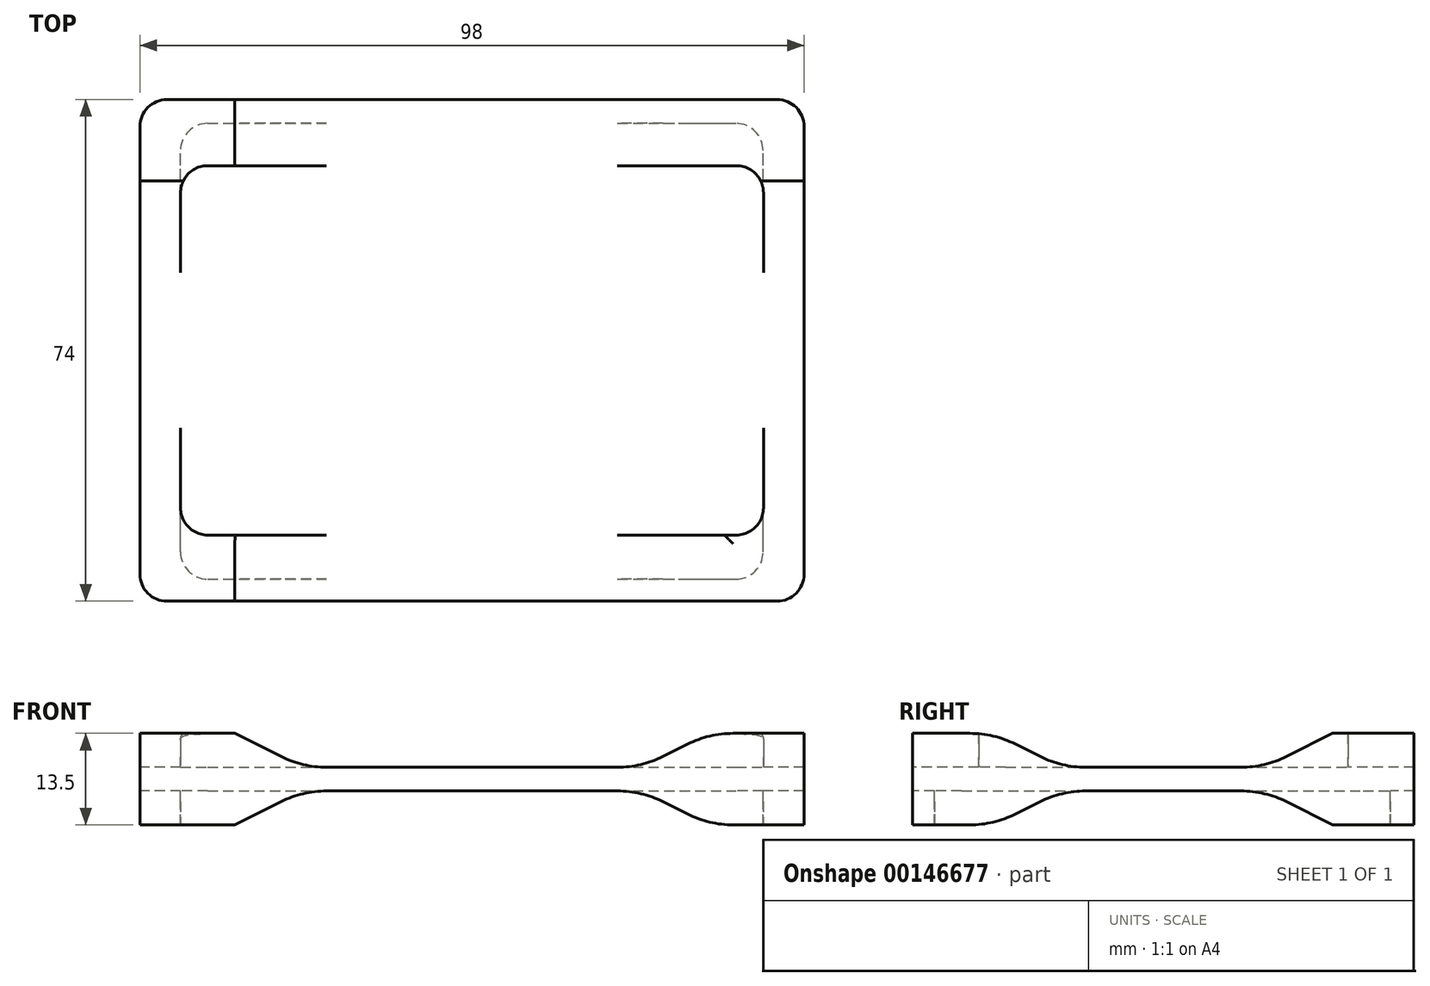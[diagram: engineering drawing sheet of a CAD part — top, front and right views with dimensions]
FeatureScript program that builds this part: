
annotation { "Feature Type Name" : "Feature", "Feature Type Description" : "" }
export const myFeature = defineFeature(function(context is Context, id is Id, definition is map)
    precondition{}
    {
        {
            var Q0;
            Q0=qCreatedBy(makeId("Top.planeOp"),FACE);
            var sketch = newSketch(context, id + "F0", { "sketchPlane" : qUnion([Q0])});
            skLineSegment(sketch, "E0.bottom", {"start": v(4, 0) * mm, "end": v(82, 0) * mm});
            skLineSegment(sketch, "E0.top", {"start": v(4, 54.5) * mm, "end": v(82, 54.5) * mm});
            skLineSegment(sketch, "E0.left", {"start": v(0, 4) * mm, "end": v(0, 50.5) * mm});
            skLineSegment(sketch, "E0.right", {"start": v(86, 4) * mm, "end": v(86, 50.5) * mm});
            skPoint(sketch, "E1.visualSharp", {"position": v(0, 54.5) * mm});
            skArc(sketch, "E1.filletArc", {"start": v(4, 54.5) * mm, "mid": v(1.17, 53.33) * mm, "end": v(0, 50.5) * mm});
            skPoint(sketch, "E2.visualSharp", {"position": v(86, 54.5) * mm});
            skArc(sketch, "E2.filletArc", {"start": v(86, 50.5) * mm, "mid": v(84.83, 53.33) * mm, "end": v(82, 54.5) * mm});
            skPoint(sketch, "E3.visualSharp", {"position": v(86, 0) * mm});
            skArc(sketch, "E3.filletArc", {"start": v(82, 0) * mm, "mid": v(84.83, 1.17) * mm, "end": v(86, 4) * mm});
            skPoint(sketch, "E4.visualSharp", {"position": v(0, 0) * mm});
            skArc(sketch, "E4.filletArc", {"start": v(0, 4) * mm, "mid": v(1.17, 1.17) * mm, "end": v(4, 0) * mm});
            skSolve(sketch);
        }
        {
            var Q0;
            Q0=qCreatedBy(makeId("Top.planeOp"),FACE);
            var sketch = newSketch(context, id + "F1", { "sketchPlane" : qUnion([Q0])});
            skLineSegment(sketch, "E5", {"start": v(0, 0) * mm, "end": v(0, -9.75) * mm, "construction": true});
            skLineSegment(sketch, "E6", {"start": v(0, -9.75) * mm, "end": v(-6, -9.75) * mm, "construction": true});
            skLineSegment(sketch, "E7.bottom", {"start": v(-2, -9.75) * mm, "end": v(88, -9.75) * mm});
            skLineSegment(sketch, "E7.top", {"start": v(-2, 64.25) * mm, "end": v(88, 64.25) * mm});
            skLineSegment(sketch, "E7.left", {"start": v(-6, -5.75) * mm, "end": v(-6, 60.25) * mm});
            skLineSegment(sketch, "E7.right", {"start": v(92, -5.75) * mm, "end": v(92, 60.25) * mm});
            skPoint(sketch, "E8.0", {"position": v(86, 54.5) * mm});
            skLineSegment(sketch, "E9", {"start": v(86, 54.5) * mm, "end": v(86, 64.25) * mm, "construction": true});
            skLineSegment(sketch, "E10", {"start": v(86, 64.25) * mm, "end": v(92, 64.25) * mm, "construction": true});
            skPoint(sketch, "E11.visualSharp", {"position": v(-6, 64.25) * mm});
            skArc(sketch, "E11.filletArc", {"start": v(-2, 64.25) * mm, "mid": v(-4.83, 63.08) * mm, "end": v(-6, 60.25) * mm});
            skPoint(sketch, "E12.visualSharp", {"position": v(92, 64.25) * mm});
            skArc(sketch, "E12.filletArc", {"start": v(92, 60.25) * mm, "mid": v(90.83, 63.08) * mm, "end": v(88, 64.25) * mm});
            skPoint(sketch, "E13.visualSharp", {"position": v(92, -9.75) * mm});
            skArc(sketch, "E13.filletArc", {"start": v(88, -9.75) * mm, "mid": v(90.83, -8.58) * mm, "end": v(92, -5.75) * mm});
            skPoint(sketch, "E14.visualSharp", {"position": v(-6, -9.75) * mm});
            skArc(sketch, "E14.filletArc", {"start": v(-6, -5.75) * mm, "mid": v(-4.83, -8.58) * mm, "end": v(-2, -9.75) * mm});
            skSolve(sketch);
        }
        {
            var Q0;
            Q0=makeQuery(id+"F1.imprint","IMPRINT",FACE,{"disambiguationData":[TD([[makeQuery(id+"F1.imprint","IMPRINT",EDGE,{"derivedFrom":sQuery(id+"F1.wireOp",EDGE,"E7.bottom")}),1.0]])]});
            extrude(context, id + "F2", {"entities" : qUnion([Q0]), "oppositeDirection" : true, "depth" : 8.5 * mm, "hasSecondDirection" : true, "secondDirectionOppositeDirection" : false, "secondDirectionDepth" : 5 * mm});
        }
        {
            var Q0;
            Q0=makeQuery(id+"F0.imprint","IMPRINT",FACE,{"disambiguationData":[TD([[makeQuery(id+"F0.imprint","IMPRINT",EDGE,{"derivedFrom":sQuery(id+"F0.wireOp",EDGE,"E0.bottom")}),1.0]])]});
            extrude(context, id + "F3", {"entities" : qUnion([Q0]), "operationType" : NewBodyOperationType.REMOVE, "depth" : 5 * mm});
        }
        {
            var Q0;
            Q0=qCreatedBy(makeId("Top.planeOp"),FACE);
            var sketch = newSketch(context, id + "F4", { "sketchPlane" : qUnion([Q0])});
            skLineSegment(sketch, "E15", {"start": v(0, 0) * mm, "end": v(0, -6.5) * mm, "construction": true});
            skLineSegment(sketch, "E16", {"start": v(85.95, 54.24) * mm, "end": v(85.95, 60.74) * mm, "construction": true});
            skLineSegment(sketch, "E17.bottom", {"start": v(4, -6.5) * mm, "end": v(81.95, -6.5) * mm});
            skLineSegment(sketch, "E17.top", {"start": v(4, 60.74) * mm, "end": v(81.95, 60.74) * mm});
            skLineSegment(sketch, "E17.left", {"start": v(0, -2.5) * mm, "end": v(0, 56.74) * mm});
            skLineSegment(sketch, "E17.right", {"start": v(85.95, -2.5) * mm, "end": v(85.95, 56.74) * mm});
            skPoint(sketch, "E18.visualSharp", {"position": v(0, 60.74) * mm});
            skArc(sketch, "E18.filletArc", {"start": v(4, 60.74) * mm, "mid": v(1.17, 59.57) * mm, "end": v(0, 56.74) * mm});
            skPoint(sketch, "E19.visualSharp", {"position": v(85.95, 60.74) * mm});
            skArc(sketch, "E19.filletArc", {"start": v(85.95, 56.74) * mm, "mid": v(84.78, 59.57) * mm, "end": v(81.95, 60.74) * mm});
            skPoint(sketch, "E20.visualSharp", {"position": v(85.95, -6.5) * mm});
            skArc(sketch, "E20.filletArc", {"start": v(81.95, -6.5) * mm, "mid": v(84.78, -5.33) * mm, "end": v(85.95, -2.5) * mm});
            skPoint(sketch, "E21.visualSharp", {"position": v(0, -6.5) * mm});
            skArc(sketch, "E21.filletArc", {"start": v(0, -2.5) * mm, "mid": v(1.17, -5.33) * mm, "end": v(4, -6.5) * mm});
            skSolve(sketch);
        }
        {
            var Q0;
            Q0=makeQuery(id+"F4.imprint","IMPRINT",FACE,{"disambiguationData":[TD([[makeQuery(id+"F4.imprint","IMPRINT",EDGE,{"derivedFrom":sQuery(id+"F4.wireOp",EDGE,"E17.bottom")}),1.0]])]});
            extrude(context, id + "F5", {"entities" : qUnion([Q0]), "operationType" : NewBodyOperationType.REMOVE, "oppositeDirection" : true, "depth" : 8.5 * mm, "hasSecondDirection" : true, "secondDirectionOppositeDirection" : true, "secondDirectionDepth" : 3.5 * mm});
        }
        {
            var Q0;
            Q0=makeQuery(id+"F2.opExtrude","SWEPT_FACE",FACE,{"disambiguationData":[OSD([sQuery(id+"F1.wireOp",EDGE,"E7.left")])]});
            var sketch = newSketch(context, id + "F6", { "sketchPlane" : qUnion([Q0])});
            skLineSegment(sketch, "E22.0", {"start": v(5.75, 5) * mm, "end": v(-60.25, 5) * mm});
            skLineSegment(sketch, "E23", {"start": v(-27.25, 5) * mm, "end": v(-27.25, 0) * mm, "construction": true});
            skLineSegment(sketch, "E24", {"start": v(-27.25, 0) * mm, "end": v(-12.25, 0) * mm});
            skLineSegment(sketch, "E25", {"start": v(-27.25, 5) * mm, "end": v(-2.25, 5) * mm});
            skLineSegment(sketch, "E26", {"start": v(-2.25, 5) * mm, "end": v(-12.25, 0) * mm});
            skLineSegment(sketch, "E27.MirrorCS", {"start": v(-27.25, 5) * mm, "end": v(-52.25, 5) * mm});
            skLineSegment(sketch, "E28.MirrorCS", {"start": v(-52.25, 5) * mm, "end": v(-42.25, 0) * mm});
            skLineSegment(sketch, "E29.MirrorCS", {"start": v(-27.25, 0) * mm, "end": v(-42.25, 0) * mm});
            skLineSegment(sketch, "E30.0", {"start": v(5.75, -8.5) * mm, "end": v(5.75, 5) * mm});
            skLineSegment(sketch, "E31", {"start": v(5.75, -1.75) * mm, "end": v(-44.25, -1.75) * mm, "construction": true});
            skLineSegment(sketch, "E32.MirrorCS", {"start": v(-27.25, -8.5) * mm, "end": v(-52.25, -8.5) * mm});
            skLineSegment(sketch, "E33.MirrorCS", {"start": v(-2.25, -8.5) * mm, "end": v(-12.25, -3.5) * mm});
            skLineSegment(sketch, "E34.MirrorCS", {"start": v(-27.25, -8.5) * mm, "end": v(-2.25, -8.5) * mm});
            skLineSegment(sketch, "E35.MirrorCS", {"start": v(-27.25, -3.5) * mm, "end": v(-12.25, -3.5) * mm});
            skLineSegment(sketch, "E36.MirrorCS", {"start": v(-27.25, -3.5) * mm, "end": v(-42.25, -3.5) * mm});
            skLineSegment(sketch, "E37.MirrorCS", {"start": v(-52.25, -8.5) * mm, "end": v(-42.25, -3.5) * mm});
            skSolve(sketch);
        }
        {
            var Q0;
            Q0=makeQuery(id+"F6.imprint","IMPRINT",FACE,{"disambiguationData":[TD([[makeQuery(id+"F6.imprint","IMPRINT",EDGE,{"derivedFrom":sQuery(id+"F6.wireOp",EDGE,"E32.MirrorCS")}),-1.0]])]});
            var Q1;
            Q1=makeQuery(id+"F6.imprint","IMPRINT",FACE,{"disambiguationData":[TD([[makeQuery(id+"F6.imprint","IMPRINT",EDGE,{"derivedFrom":sQuery(id+"F6.wireOp",EDGE,"E24")}),1.0]])]});
            extrude(context, id + "F7", {"entities" : qUnion([Q0, Q1]), "operationType" : NewBodyOperationType.REMOVE, "endBound" : BoundingType.THROUGH_ALL, "oppositeDirection" : true, "depth" : 25 * mm});
        }
        {
            var Q0;
            Q0=makeQuery(id+"F2.opExtrude","SWEPT_FACE",FACE,{"disambiguationData":[OSD([sQuery(id+"F1.wireOp",EDGE,"E7.bottom")])]});
            var sketch = newSketch(context, id + "F8", { "sketchPlane" : qUnion([Q0])});
            skLineSegment(sketch, "E38.0", {"start": v(-2, 5) * mm, "end": v(88, 5) * mm});
            skLineSegment(sketch, "E39", {"start": v(43, 5) * mm, "end": v(43, 0) * mm, "construction": true});
            skLineSegment(sketch, "E40", {"start": v(43, 0) * mm, "end": v(68, 0) * mm});
            skLineSegment(sketch, "E41", {"start": v(68, 0) * mm, "end": v(78, 5) * mm});
            skLineSegment(sketch, "E42.MirrorCS", {"start": v(18, 0) * mm, "end": v(8, 5) * mm});
            skLineSegment(sketch, "E43.MirrorCS", {"start": v(43, 0) * mm, "end": v(18, 0) * mm});
            skLineSegment(sketch, "E44", {"start": v(78, 5) * mm, "end": v(8, 5) * mm});
            skLineSegment(sketch, "E45.0", {"start": v(88, -8.5) * mm, "end": v(88, 5) * mm});
            skLineSegment(sketch, "E46", {"start": v(88, -1.75) * mm, "end": v(73, -1.75) * mm, "construction": true});
            skLineSegment(sketch, "E47.MirrorCS", {"start": v(78, -8.5) * mm, "end": v(8, -8.5) * mm});
            skLineSegment(sketch, "E48.MirrorCS", {"start": v(18, -3.5) * mm, "end": v(8, -8.5) * mm});
            skLineSegment(sketch, "E49.MirrorCS", {"start": v(43, -3.5) * mm, "end": v(18, -3.5) * mm});
            skLineSegment(sketch, "E50.MirrorCS", {"start": v(43, -3.5) * mm, "end": v(68, -3.5) * mm});
            skLineSegment(sketch, "E51.MirrorCS", {"start": v(68, -3.5) * mm, "end": v(78, -8.5) * mm});
            skSolve(sketch);
        }
        {
            var Q0;
            Q0=makeQuery(id+"F8.imprint","IMPRINT",FACE,{"disambiguationData":[TD([[makeQuery(id+"F8.imprint","IMPRINT",EDGE,{"derivedFrom":sQuery(id+"F8.wireOp",EDGE,"E47.MirrorCS")}),1.0]])]});
            var Q1;
            Q1=makeQuery(id+"F8.imprint","IMPRINT",FACE,{"disambiguationData":[TD([[makeQuery(id+"F8.imprint","IMPRINT",EDGE,{"derivedFrom":sQuery(id+"F8.wireOp",EDGE,"E40")}),1.0]])]});
            extrude(context, id + "F9", {"entities" : qUnion([Q0, Q1]), "operationType" : NewBodyOperationType.REMOVE, "endBound" : BoundingType.THROUGH_ALL, "oppositeDirection" : true, "depth" : 50 * mm});
        }
        {
            var Q0;
            Q0=makeQuery(id+"F7.boolean.opBoolean","COPY",EDGE,{"disambiguationData":[OD(1.0)],"derivedFrom":makeQuery(id+"F7.opExtrude","SWEPT_EDGE",EDGE,{"disambiguationData":[OSD([sQuery(id+"F6.wireOp",EDGE,"E36.MirrorCS"),sQuery(id+"F6.wireOp",EDGE,"E37.MirrorCS")])]})});
            var Q1;
            Q1=makeQuery(id+"F7.boolean.opBoolean","COPY",EDGE,{"disambiguationData":[OD(1.0)],"derivedFrom":makeQuery(id+"F7.opExtrude","SWEPT_EDGE",EDGE,{"disambiguationData":[OSD([sQuery(id+"F6.wireOp",EDGE,"E33.MirrorCS"),sQuery(id+"F6.wireOp",EDGE,"E35.MirrorCS")])]})});
            var Q2;
            Q2=makeQuery(id+"F7.boolean.opBoolean","COPY",EDGE,{"disambiguationData":[OD(1.0)],"derivedFrom":makeQuery(id+"F7.opExtrude","SWEPT_EDGE",EDGE,{"disambiguationData":[OSD([sQuery(id+"F1.wireOp",EDGE,"E7.left"),sQuery(id+"F6.wireOp",EDGE,"E33.MirrorCS"),sQuery(id+"F6.wireOp",EDGE,"E34.MirrorCS")])]})});
            var Q3;
            Q3=makeQuery(id+"F7.boolean.opBoolean","COPY",EDGE,{"disambiguationData":[OD(1.0)],"derivedFrom":makeQuery(id+"F7.opExtrude","SWEPT_EDGE",EDGE,{"disambiguationData":[OSD([sQuery(id+"F1.wireOp",EDGE,"E7.left"),sQuery(id+"F6.wireOp",EDGE,"E32.MirrorCS"),sQuery(id+"F6.wireOp",EDGE,"E37.MirrorCS")])]})});
            var Q4;
            Q4=makeQuery(id+"F9.boolean.opBoolean","COPY",EDGE,{"disambiguationData":[OD(1.0)],"derivedFrom":makeQuery(id+"F9.opExtrude","SWEPT_EDGE",EDGE,{"disambiguationData":[OSD([sQuery(id+"F1.wireOp",EDGE,"E7.bottom"),sQuery(id+"F8.wireOp",EDGE,"E47.MirrorCS"),sQuery(id+"F8.wireOp",EDGE,"E51.MirrorCS")])]})});
            var Q5;
            Q5=makeQuery(id+"F9.boolean.opBoolean","COPY",EDGE,{"disambiguationData":[OD(1.0)],"derivedFrom":makeQuery(id+"F9.opExtrude","SWEPT_EDGE",EDGE,{"disambiguationData":[OSD([sQuery(id+"F8.wireOp",EDGE,"E50.MirrorCS"),sQuery(id+"F8.wireOp",EDGE,"E51.MirrorCS")])]})});
            var Q6;
            Q6=makeQuery(id+"F9.boolean.opBoolean","COPY",EDGE,{"disambiguationData":[OD(1.0)],"derivedFrom":makeQuery(id+"F9.opExtrude","SWEPT_EDGE",EDGE,{"disambiguationData":[OSD([sQuery(id+"F8.wireOp",EDGE,"E48.MirrorCS"),sQuery(id+"F8.wireOp",EDGE,"E49.MirrorCS")])]})});
            var Q7;
            Q7=makeQuery(id+"F9.boolean.opBoolean","COPY",EDGE,{"disambiguationData":[OD(1.0)],"derivedFrom":makeQuery(id+"F9.opExtrude","SWEPT_EDGE",EDGE,{"disambiguationData":[OSD([sQuery(id+"F1.wireOp",EDGE,"E7.bottom"),sQuery(id+"F8.wireOp",EDGE,"E47.MirrorCS"),sQuery(id+"F8.wireOp",EDGE,"E48.MirrorCS")])]})});
            var Q8;
            Q8=makeQuery(id+"F7.boolean.opBoolean","COPY",EDGE,{"disambiguationData":[OD(0.0)],"derivedFrom":makeQuery(id+"F7.opExtrude","SWEPT_EDGE",EDGE,{"disambiguationData":[OSD([sQuery(id+"F1.wireOp",EDGE,"E7.left"),sQuery(id+"F6.wireOp",EDGE,"E32.MirrorCS"),sQuery(id+"F6.wireOp",EDGE,"E37.MirrorCS")])]})});
            var Q9;
            Q9=makeQuery(id+"F7.boolean.opBoolean","COPY",EDGE,{"disambiguationData":[OD(0.0)],"derivedFrom":makeQuery(id+"F7.opExtrude","SWEPT_EDGE",EDGE,{"disambiguationData":[OSD([sQuery(id+"F6.wireOp",EDGE,"E36.MirrorCS"),sQuery(id+"F6.wireOp",EDGE,"E37.MirrorCS")])]})});
            var Q10;
            Q10=makeQuery(id+"F7.boolean.opBoolean","COPY",EDGE,{"disambiguationData":[OD(0.0)],"derivedFrom":makeQuery(id+"F7.opExtrude","SWEPT_EDGE",EDGE,{"disambiguationData":[OSD([sQuery(id+"F6.wireOp",EDGE,"E33.MirrorCS"),sQuery(id+"F6.wireOp",EDGE,"E35.MirrorCS")])]})});
            var Q11;
            Q11=makeQuery(id+"F7.boolean.opBoolean","COPY",EDGE,{"disambiguationData":[OD(0.0)],"derivedFrom":makeQuery(id+"F7.opExtrude","SWEPT_EDGE",EDGE,{"disambiguationData":[OSD([sQuery(id+"F1.wireOp",EDGE,"E7.left"),sQuery(id+"F6.wireOp",EDGE,"E33.MirrorCS"),sQuery(id+"F6.wireOp",EDGE,"E34.MirrorCS")])]})});
            var Q12;
            Q12=makeQuery(id+"F9.boolean.opBoolean","COPY",EDGE,{"disambiguationData":[OD(0.0)],"derivedFrom":makeQuery(id+"F9.opExtrude","SWEPT_EDGE",EDGE,{"disambiguationData":[OSD([sQuery(id+"F1.wireOp",EDGE,"E7.bottom"),sQuery(id+"F8.wireOp",EDGE,"E47.MirrorCS"),sQuery(id+"F8.wireOp",EDGE,"E48.MirrorCS")])]})});
            var Q13;
            Q13=makeQuery(id+"F9.boolean.opBoolean","COPY",EDGE,{"disambiguationData":[OD(0.0)],"derivedFrom":makeQuery(id+"F9.opExtrude","SWEPT_EDGE",EDGE,{"disambiguationData":[OSD([sQuery(id+"F8.wireOp",EDGE,"E48.MirrorCS"),sQuery(id+"F8.wireOp",EDGE,"E49.MirrorCS")])]})});
            var Q14;
            Q14=makeQuery(id+"F9.boolean.opBoolean","COPY",EDGE,{"disambiguationData":[OD(0.0)],"derivedFrom":makeQuery(id+"F9.opExtrude","SWEPT_EDGE",EDGE,{"disambiguationData":[OSD([sQuery(id+"F8.wireOp",EDGE,"E50.MirrorCS"),sQuery(id+"F8.wireOp",EDGE,"E51.MirrorCS")])]})});
            var Q15;
            Q15=makeQuery(id+"F9.boolean.opBoolean","COPY",EDGE,{"disambiguationData":[OD(0.0)],"derivedFrom":makeQuery(id+"F9.opExtrude","SWEPT_EDGE",EDGE,{"disambiguationData":[OSD([sQuery(id+"F1.wireOp",EDGE,"E7.bottom"),sQuery(id+"F8.wireOp",EDGE,"E47.MirrorCS"),sQuery(id+"F8.wireOp",EDGE,"E51.MirrorCS")])]})});
            var Q16;
            Q16=makeQuery(id+"F7.boolean.opBoolean","COPY",EDGE,{"disambiguationData":[OD(1.0)],"derivedFrom":makeQuery(id+"F7.opExtrude","SWEPT_EDGE",EDGE,{"disambiguationData":[OSD([sQuery(id+"F6.wireOp",EDGE,"E24"),sQuery(id+"F6.wireOp",EDGE,"E26")])]})});
            var Q17;
            Q17=makeQuery(id+"F7.boolean.opBoolean","COPY",EDGE,{"disambiguationData":[OD(1.0)],"derivedFrom":makeQuery(id+"F7.opExtrude","SWEPT_EDGE",EDGE,{"disambiguationData":[OSD([sQuery(id+"F6.wireOp",EDGE,"E22.0"),sQuery(id+"F6.wireOp",EDGE,"E25"),sQuery(id+"F6.wireOp",EDGE,"E26")])]})});
            var Q18;
            Q18=makeQuery(id+"F9.boolean.opBoolean","COPY",EDGE,{"disambiguationData":[OD(0.0)],"derivedFrom":makeQuery(id+"F9.opExtrude","SWEPT_EDGE",EDGE,{"disambiguationData":[OSD([sQuery(id+"F8.wireOp",EDGE,"E38.0"),sQuery(id+"F8.wireOp",EDGE,"E41"),sQuery(id+"F8.wireOp",EDGE,"E44")])]})});
            var Q19;
            Q19=makeQuery(id+"F9.boolean.opBoolean","COPY",EDGE,{"disambiguationData":[OD(0.0)],"derivedFrom":makeQuery(id+"F9.opExtrude","SWEPT_EDGE",EDGE,{"disambiguationData":[OSD([sQuery(id+"F8.wireOp",EDGE,"E40"),sQuery(id+"F8.wireOp",EDGE,"E41")])]})});
            var Q20;
            Q20=makeQuery(id+"F9.boolean.opBoolean","COPY",EDGE,{"disambiguationData":[OD(0.0)],"derivedFrom":makeQuery(id+"F9.opExtrude","SWEPT_EDGE",EDGE,{"disambiguationData":[OSD([sQuery(id+"F8.wireOp",EDGE,"E42.MirrorCS"),sQuery(id+"F8.wireOp",EDGE,"E43.MirrorCS")])]})});
            var Q21;
            Q21=makeQuery(id+"F9.boolean.opBoolean","COPY",EDGE,{"disambiguationData":[OD(0.0)],"derivedFrom":makeQuery(id+"F9.opExtrude","SWEPT_EDGE",EDGE,{"disambiguationData":[OSD([sQuery(id+"F8.wireOp",EDGE,"E38.0"),sQuery(id+"F8.wireOp",EDGE,"E42.MirrorCS"),sQuery(id+"F8.wireOp",EDGE,"E44")])]})});
            var Q22;
            Q22=makeQuery(id+"F7.boolean.opBoolean","COPY",EDGE,{"disambiguationData":[OD(0.0)],"derivedFrom":makeQuery(id+"F7.opExtrude","SWEPT_EDGE",EDGE,{"disambiguationData":[OSD([sQuery(id+"F6.wireOp",EDGE,"E22.0"),sQuery(id+"F6.wireOp",EDGE,"E25"),sQuery(id+"F6.wireOp",EDGE,"E26")])]})});
            var Q23;
            Q23=makeQuery(id+"F7.boolean.opBoolean","COPY",EDGE,{"disambiguationData":[OD(0.0)],"derivedFrom":makeQuery(id+"F7.opExtrude","SWEPT_EDGE",EDGE,{"disambiguationData":[OSD([sQuery(id+"F6.wireOp",EDGE,"E24"),sQuery(id+"F6.wireOp",EDGE,"E26")])]})});
            var Q24;
            Q24=makeQuery(id+"F7.boolean.opBoolean","COPY",EDGE,{"disambiguationData":[OD(0.0)],"derivedFrom":makeQuery(id+"F7.opExtrude","SWEPT_EDGE",EDGE,{"disambiguationData":[OSD([sQuery(id+"F6.wireOp",EDGE,"E28.MirrorCS"),sQuery(id+"F6.wireOp",EDGE,"E29.MirrorCS")])]})});
            var Q25;
            Q25=makeQuery(id+"F7.boolean.opBoolean","COPY",EDGE,{"disambiguationData":[OD(0.0)],"derivedFrom":makeQuery(id+"F7.opExtrude","SWEPT_EDGE",EDGE,{"disambiguationData":[OSD([sQuery(id+"F6.wireOp",EDGE,"E22.0"),sQuery(id+"F6.wireOp",EDGE,"E27.MirrorCS"),sQuery(id+"F6.wireOp",EDGE,"E28.MirrorCS")])]})});
            var Q26;
            Q26=makeQuery(id+"F9.boolean.opBoolean","COPY",EDGE,{"disambiguationData":[OD(1.0)],"derivedFrom":makeQuery(id+"F9.opExtrude","SWEPT_EDGE",EDGE,{"disambiguationData":[OSD([sQuery(id+"F8.wireOp",EDGE,"E38.0"),sQuery(id+"F8.wireOp",EDGE,"E42.MirrorCS"),sQuery(id+"F8.wireOp",EDGE,"E44")])]})});
            var Q27;
            Q27=makeQuery(id+"F9.boolean.opBoolean","COPY",EDGE,{"disambiguationData":[OD(1.0)],"derivedFrom":makeQuery(id+"F9.opExtrude","SWEPT_EDGE",EDGE,{"disambiguationData":[OSD([sQuery(id+"F8.wireOp",EDGE,"E42.MirrorCS"),sQuery(id+"F8.wireOp",EDGE,"E43.MirrorCS")])]})});
            var Q28;
            Q28=makeQuery(id+"F9.boolean.opBoolean","COPY",EDGE,{"disambiguationData":[OD(1.0)],"derivedFrom":makeQuery(id+"F9.opExtrude","SWEPT_EDGE",EDGE,{"disambiguationData":[OSD([sQuery(id+"F8.wireOp",EDGE,"E40"),sQuery(id+"F8.wireOp",EDGE,"E41")])]})});
            var Q29;
            Q29=makeQuery(id+"F9.boolean.opBoolean","COPY",EDGE,{"disambiguationData":[OD(1.0)],"derivedFrom":makeQuery(id+"F9.opExtrude","SWEPT_EDGE",EDGE,{"disambiguationData":[OSD([sQuery(id+"F8.wireOp",EDGE,"E38.0"),sQuery(id+"F8.wireOp",EDGE,"E41"),sQuery(id+"F8.wireOp",EDGE,"E44")])]})});
            var Q30;
            Q30=makeQuery(id+"F7.boolean.opBoolean","COPY",EDGE,{"disambiguationData":[OD(1.0)],"derivedFrom":makeQuery(id+"F7.opExtrude","SWEPT_EDGE",EDGE,{"disambiguationData":[OSD([sQuery(id+"F6.wireOp",EDGE,"E22.0"),sQuery(id+"F6.wireOp",EDGE,"E27.MirrorCS"),sQuery(id+"F6.wireOp",EDGE,"E28.MirrorCS")])]})});
            var Q31;
            Q31=makeQuery(id+"F7.boolean.opBoolean","COPY",EDGE,{"disambiguationData":[OD(1.0)],"derivedFrom":makeQuery(id+"F7.opExtrude","SWEPT_EDGE",EDGE,{"disambiguationData":[OSD([sQuery(id+"F6.wireOp",EDGE,"E28.MirrorCS"),sQuery(id+"F6.wireOp",EDGE,"E29.MirrorCS")])]})});
            fillet(context, id + "F10", {"entities" : qUnion([Q0, Q1, Q2, Q3, Q4, Q5, Q6, Q7, Q8, Q9, Q10, Q11, Q12, Q13, Q14, Q15, Q16, Q17, Q18, Q19, Q20, Q21, Q22, Q23, Q24, Q25, Q26, Q27, Q28, Q29, Q30, Q31]), "radius" : 15 * mm, "tangentPropagation" : true, "allowEdgeOverflow" : false});
        }
    });
